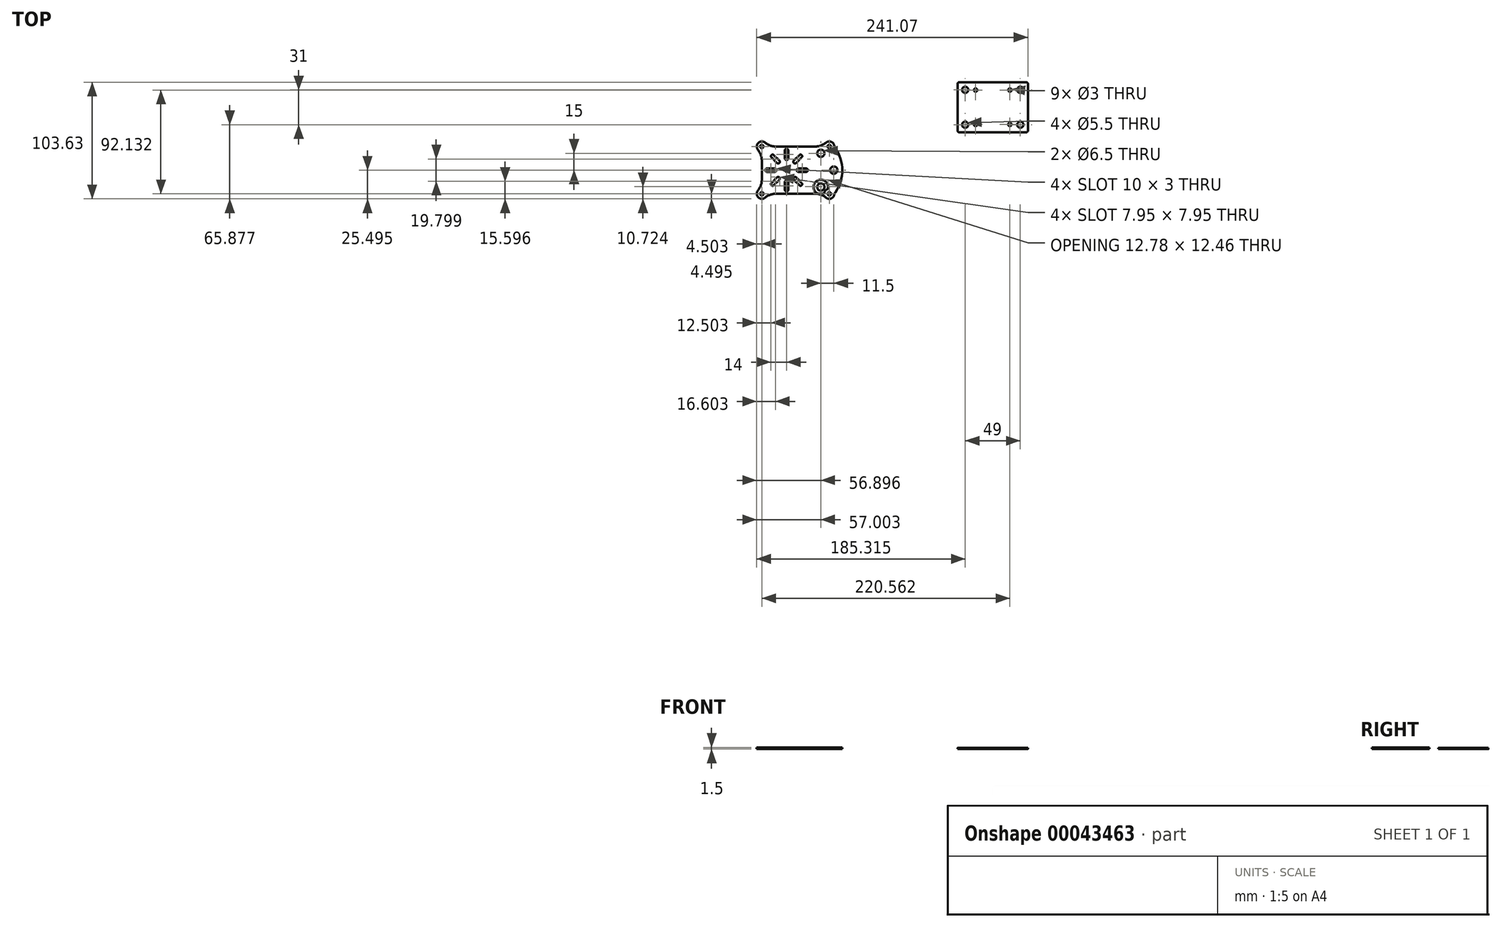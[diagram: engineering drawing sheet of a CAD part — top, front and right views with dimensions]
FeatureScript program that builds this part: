
annotation { "Feature Type Name" : "Feature", "Feature Type Description" : "" }
export const myFeature = defineFeature(function(context is Context, id is Id, definition is map)
    precondition{}
    {
        {
            var Q0;
            Q0=qCreatedBy(makeId("Top.planeOp"),FACE);
            var sketch = newSketch(context, id + "F0", { "sketchPlane" : qUnion([Q0])});
            skCircle(sketch, "E0", {"center": v(-51.28, 40.9) * mm, "radius": 1.5 * mm});
            skCircle(sketch, "E1", {"center": v(8.72, 40.9) * mm, "radius": 1.5 * mm});
            skCircle(sketch, "E2", {"center": v(-51.28, -1.1) * mm, "radius": 1.5 * mm});
            skCircle(sketch, "E3", {"center": v(8.72, -1.1) * mm, "radius": 1.5 * mm});
            skCircle(sketch, "E4", {"center": v(-29.28, 19.9) * mm, "radius": 27 * mm});
            skLineSegment(sketch, "E5", {"start": v(-51.28, 40.9) * mm, "end": v(-51.28, -1.1) * mm});
            skLineSegment(sketch, "E6", {"start": v(-51.28, 19.9) * mm, "end": v(20.22, 19.9) * mm});
            skCircle(sketch, "E7", {"center": v(12.72, 19.9) * mm, "radius": 3.25 * mm});
            skCircle(sketch, "E8", {"center": v(12.72, 19.9) * mm, "radius": 6.5 * mm});
            skCircle(sketch, "E9", {"center": v(-51.28, 40.9) * mm, "radius": 4.5 * mm});
            skCircle(sketch, "E10", {"center": v(-51.28, -1.1) * mm, "radius": 4.5 * mm});
            skCircle(sketch, "E11", {"center": v(8.72, -1.1) * mm, "radius": 4.5 * mm});
            skCircle(sketch, "E12", {"center": v(8.72, 40.9) * mm, "radius": 4.5 * mm});
            skLineSegment(sketch, "E13", {"start": v(-51.28, 40.9) * mm, "end": v(8.72, 40.9) * mm});
            skLineSegment(sketch, "E14", {"start": v(8.72, 40.9) * mm, "end": v(13.22, 40.9) * mm});
            skLineSegment(sketch, "E15", {"start": v(8.72, -1.1) * mm, "end": v(13.22, -1.1) * mm});
            skArc(sketch, "E16", {"start": v(13.22, -1.1) * mm, "mid": v(20.22, 19.9) * mm, "end": v(13.22, 40.9) * mm});
            skLineSegment(sketch, "E17", {"start": v(-51.28, -1.1) * mm, "end": v(8.72, -1.1) * mm});
            skCircle(sketch, "E18", {"center": v(20.37, 43.8) * mm, "radius": 7.5 * mm});
            skCircle(sketch, "E19", {"center": v(20.37, -4) * mm, "radius": 7.5 * mm});
            skCircle(sketch, "E20", {"center": v(-66.28, 28.44) * mm, "radius": 15 * mm});
            skCircle(sketch, "E21", {"center": v(-66.28, 11.36) * mm, "radius": 15 * mm});
            skCircle(sketch, "E22", {"center": v(-38.82, -16.1) * mm, "radius": 15 * mm});
            skCircle(sketch, "E23", {"center": v(-3.74, -16.1) * mm, "radius": 15 * mm});
            skCircle(sketch, "E24", {"center": v(-3.74, 55.9) * mm, "radius": 15 * mm});
            skCircle(sketch, "E25", {"center": v(-38.82, 55.9) * mm, "radius": 15 * mm});
            skLineSegment(sketch, "E26", {"start": v(-29.28, 19.9) * mm, "end": v(-29.28, 46.9) * mm});
            skLineSegment(sketch, "E27.bottom", {"start": v(-38.28, 19.9) * mm, "end": v(-48.28, 19.9) * mm});
            skLineSegment(sketch, "E27.top", {"start": v(-39.78, 21.4) * mm, "end": v(-46.78, 21.4) * mm});
            skLineSegment(sketch, "E27.left", {"start": v(-38.28, 19.9) * mm, "end": v(-38.28, 19.9) * mm});
            skLineSegment(sketch, "E27.right", {"start": v(-48.28, 19.9) * mm, "end": v(-48.28, 19.9) * mm});
            skLineSegment(sketch, "E28.bottom", {"start": v(-29.28, 38.9) * mm, "end": v(-29.28, 38.9) * mm});
            skLineSegment(sketch, "E28.top", {"start": v(-29.28, 28.9) * mm, "end": v(-29.28, 28.9) * mm});
            skLineSegment(sketch, "E28.left", {"start": v(-29.28, 38.9) * mm, "end": v(-29.28, 28.9) * mm});
            skLineSegment(sketch, "E28.right", {"start": v(-30.78, 37.4) * mm, "end": v(-30.78, 30.4) * mm});
            skLineSegment(sketch, "E29", {"start": v(-35.64, 26.26) * mm, "end": v(-35.64, 26.26) * mm});
            skLineSegment(sketch, "E30", {"start": v(-35.64, 28.38) * mm, "end": v(-40.6, 33.33) * mm});
            skLineSegment(sketch, "E31", {"start": v(-42.71, 33.33) * mm, "end": v(-42.71, 33.33) * mm});
            skLineSegment(sketch, "E32", {"start": v(-42.71, 31.2) * mm, "end": v(-37.76, 26.26) * mm});
            skPoint(sketch, "E33", {"position": v(-35.64, 26.26) * mm});
            skLineSegment(sketch, "E34.MirrorCS", {"start": v(-27.78, 37.4) * mm, "end": v(-27.78, 30.4) * mm});
            skLineSegment(sketch, "E35.MirrorCS", {"start": v(-22.91, 28.38) * mm, "end": v(-17.96, 33.33) * mm});
            skLineSegment(sketch, "E36.MirrorCS", {"start": v(-15.84, 33.33) * mm, "end": v(-15.84, 33.33) * mm});
            skLineSegment(sketch, "E37.MirrorCS", {"start": v(-15.84, 31.2) * mm, "end": v(-20.8, 26.26) * mm});
            skLineSegment(sketch, "E38.MirrorCS", {"start": v(-22.91, 26.26) * mm, "end": v(-22.91, 26.26) * mm});
            skLineSegment(sketch, "E39.MirrorCS", {"start": v(-20.28, 19.9) * mm, "end": v(-20.28, 19.9) * mm});
            skLineSegment(sketch, "E40.MirrorCS", {"start": v(-18.78, 21.4) * mm, "end": v(-11.78, 21.4) * mm});
            skLineSegment(sketch, "E41.MirrorCS", {"start": v(-10.28, 19.9) * mm, "end": v(-10.28, 19.9) * mm});
            skLineSegment(sketch, "E42.MirrorCS", {"start": v(-18.78, 18.4) * mm, "end": v(-11.78, 18.4) * mm});
            skLineSegment(sketch, "E43.MirrorCS", {"start": v(-22.91, 11.41) * mm, "end": v(-17.96, 6.46) * mm});
            skLineSegment(sketch, "E44.MirrorCS", {"start": v(-15.84, 6.46) * mm, "end": v(-15.84, 6.46) * mm});
            skLineSegment(sketch, "E45.MirrorCS", {"start": v(-22.91, 13.53) * mm, "end": v(-22.91, 13.53) * mm});
            skLineSegment(sketch, "E46.MirrorCS", {"start": v(-15.84, 8.58) * mm, "end": v(-20.8, 13.53) * mm});
            skLineSegment(sketch, "E47.MirrorCS", {"start": v(-29.28, 0.9) * mm, "end": v(-29.28, 0.9) * mm});
            skLineSegment(sketch, "E48.MirrorCS", {"start": v(-27.78, 2.4) * mm, "end": v(-27.78, 9.4) * mm});
            skLineSegment(sketch, "E49.MirrorCS", {"start": v(-29.28, 10.9) * mm, "end": v(-29.28, 10.9) * mm});
            skLineSegment(sketch, "E50.MirrorCS", {"start": v(-30.78, 2.4) * mm, "end": v(-30.78, 9.4) * mm});
            skLineSegment(sketch, "E51.MirrorCS", {"start": v(-35.64, 11.41) * mm, "end": v(-40.6, 6.46) * mm});
            skLineSegment(sketch, "E52.MirrorCS", {"start": v(-42.71, 8.58) * mm, "end": v(-37.76, 13.53) * mm});
            skLineSegment(sketch, "E53.MirrorCS", {"start": v(-42.71, 6.46) * mm, "end": v(-42.71, 6.46) * mm});
            skLineSegment(sketch, "E54.MirrorCS", {"start": v(-35.64, 13.53) * mm, "end": v(-35.64, 13.53) * mm});
            skLineSegment(sketch, "E55.MirrorCS", {"start": v(-39.78, 18.4) * mm, "end": v(-46.78, 18.4) * mm});
            skCircle(sketch, "E56", {"center": v(-29.28, 19.9) * mm, "radius": 1.5 * mm});
            skPoint(sketch, "E57.visualSharp", {"position": v(-41.65, 34.4) * mm});
            skArc(sketch, "E57.filletArc", {"start": v(-40.6, 33.33) * mm, "mid": v(-41.65, 33.77) * mm, "end": v(-42.71, 33.33) * mm});
            skPoint(sketch, "E58.visualSharp", {"position": v(-43.77, 32.27) * mm});
            skArc(sketch, "E58.filletArc", {"start": v(-42.71, 33.33) * mm, "mid": v(-43.15, 32.27) * mm, "end": v(-42.71, 31.2) * mm});
            skPoint(sketch, "E59.visualSharp", {"position": v(-34.58, 27.32) * mm});
            skArc(sketch, "E59.filletArc", {"start": v(-35.64, 26.26) * mm, "mid": v(-35.2, 27.32) * mm, "end": v(-35.64, 28.38) * mm});
            skPoint(sketch, "E60.visualSharp", {"position": v(-36.7, 25.2) * mm});
            skArc(sketch, "E60.filletArc", {"start": v(-37.76, 26.26) * mm, "mid": v(-36.7, 25.82) * mm, "end": v(-35.64, 26.26) * mm});
            skPoint(sketch, "E61.visualSharp", {"position": v(-30.78, 28.9) * mm});
            skArc(sketch, "E61.filletArc", {"start": v(-30.78, 30.4) * mm, "mid": v(-30.34, 29.33) * mm, "end": v(-29.28, 28.9) * mm});
            skPoint(sketch, "E62.visualSharp", {"position": v(-27.78, 28.9) * mm});
            skArc(sketch, "E62.filletArc", {"start": v(-29.28, 28.9) * mm, "mid": v(-28.22, 29.33) * mm, "end": v(-27.78, 30.4) * mm});
            skPoint(sketch, "E63.visualSharp", {"position": v(-27.78, 38.9) * mm});
            skArc(sketch, "E63.filletArc", {"start": v(-27.78, 37.4) * mm, "mid": v(-28.22, 38.46) * mm, "end": v(-29.28, 38.9) * mm});
            skPoint(sketch, "E64.visualSharp", {"position": v(-30.78, 38.9) * mm});
            skArc(sketch, "E64.filletArc", {"start": v(-29.28, 38.9) * mm, "mid": v(-30.34, 38.46) * mm, "end": v(-30.78, 37.4) * mm});
            skPoint(sketch, "E65.visualSharp", {"position": v(-16.9, 34.4) * mm});
            skArc(sketch, "E65.filletArc", {"start": v(-15.84, 33.33) * mm, "mid": v(-16.9, 33.77) * mm, "end": v(-17.96, 33.33) * mm});
            skPoint(sketch, "E66.visualSharp", {"position": v(-14.78, 32.27) * mm});
            skArc(sketch, "E66.filletArc", {"start": v(-15.84, 31.2) * mm, "mid": v(-15.4, 32.27) * mm, "end": v(-15.84, 33.33) * mm});
            skPoint(sketch, "E67.visualSharp", {"position": v(-23.97, 27.32) * mm});
            skArc(sketch, "E67.filletArc", {"start": v(-22.91, 28.38) * mm, "mid": v(-23.35, 27.32) * mm, "end": v(-22.91, 26.26) * mm});
            skPoint(sketch, "E68.visualSharp", {"position": v(-21.85, 25.2) * mm});
            skArc(sketch, "E68.filletArc", {"start": v(-22.91, 26.26) * mm, "mid": v(-21.85, 25.82) * mm, "end": v(-20.8, 26.26) * mm});
            skPoint(sketch, "E69.visualSharp", {"position": v(-20.28, 21.4) * mm});
            skArc(sketch, "E69.filletArc", {"start": v(-18.78, 21.4) * mm, "mid": v(-19.84, 20.96) * mm, "end": v(-20.28, 19.9) * mm});
            skPoint(sketch, "E70.visualSharp", {"position": v(-20.28, 18.4) * mm});
            skArc(sketch, "E70.filletArc", {"start": v(-20.28, 19.9) * mm, "mid": v(-19.84, 18.83) * mm, "end": v(-18.78, 18.4) * mm});
            skPoint(sketch, "E71.visualSharp", {"position": v(-10.28, 21.4) * mm});
            skArc(sketch, "E71.filletArc", {"start": v(-10.28, 19.9) * mm, "mid": v(-10.72, 20.96) * mm, "end": v(-11.78, 21.4) * mm});
            skPoint(sketch, "E72.visualSharp", {"position": v(-10.28, 18.4) * mm});
            skArc(sketch, "E72.filletArc", {"start": v(-11.78, 18.4) * mm, "mid": v(-10.72, 18.83) * mm, "end": v(-10.28, 19.9) * mm});
            skPoint(sketch, "E73.visualSharp", {"position": v(-21.85, 14.6) * mm});
            skArc(sketch, "E73.filletArc", {"start": v(-20.8, 13.53) * mm, "mid": v(-21.85, 13.97) * mm, "end": v(-22.91, 13.53) * mm});
            skPoint(sketch, "E74.visualSharp", {"position": v(-23.97, 12.47) * mm});
            skArc(sketch, "E74.filletArc", {"start": v(-22.91, 13.53) * mm, "mid": v(-23.35, 12.47) * mm, "end": v(-22.91, 11.41) * mm});
            skPoint(sketch, "E75.visualSharp", {"position": v(-14.78, 7.52) * mm});
            skArc(sketch, "E75.filletArc", {"start": v(-15.84, 6.46) * mm, "mid": v(-15.4, 7.52) * mm, "end": v(-15.84, 8.58) * mm});
            skPoint(sketch, "E76.visualSharp", {"position": v(-16.9, 5.4) * mm});
            skArc(sketch, "E76.filletArc", {"start": v(-17.96, 6.46) * mm, "mid": v(-16.9, 6.02) * mm, "end": v(-15.84, 6.46) * mm});
            skPoint(sketch, "E77.visualSharp", {"position": v(-27.78, 10.9) * mm});
            skArc(sketch, "E77.filletArc", {"start": v(-27.78, 9.4) * mm, "mid": v(-28.22, 10.46) * mm, "end": v(-29.28, 10.9) * mm});
            skPoint(sketch, "E78.visualSharp", {"position": v(-30.78, 10.9) * mm});
            skArc(sketch, "E78.filletArc", {"start": v(-29.28, 10.9) * mm, "mid": v(-30.34, 10.46) * mm, "end": v(-30.78, 9.4) * mm});
            skPoint(sketch, "E79.visualSharp", {"position": v(-30.78, 0.9) * mm});
            skArc(sketch, "E79.filletArc", {"start": v(-30.78, 2.4) * mm, "mid": v(-30.34, 1.33) * mm, "end": v(-29.28, 0.9) * mm});
            skPoint(sketch, "E80.visualSharp", {"position": v(-27.78, 0.9) * mm});
            skArc(sketch, "E80.filletArc", {"start": v(-29.28, 0.9) * mm, "mid": v(-28.22, 1.33) * mm, "end": v(-27.78, 2.4) * mm});
            skPoint(sketch, "E81.visualSharp", {"position": v(-36.7, 14.6) * mm});
            skArc(sketch, "E81.filletArc", {"start": v(-35.64, 13.53) * mm, "mid": v(-36.7, 13.97) * mm, "end": v(-37.76, 13.53) * mm});
            skPoint(sketch, "E82.visualSharp", {"position": v(-34.58, 12.47) * mm});
            skArc(sketch, "E82.filletArc", {"start": v(-35.64, 11.41) * mm, "mid": v(-35.2, 12.47) * mm, "end": v(-35.64, 13.53) * mm});
            skPoint(sketch, "E83.visualSharp", {"position": v(-43.77, 7.52) * mm});
            skArc(sketch, "E83.filletArc", {"start": v(-42.71, 8.58) * mm, "mid": v(-43.15, 7.52) * mm, "end": v(-42.71, 6.46) * mm});
            skPoint(sketch, "E84.visualSharp", {"position": v(-41.65, 5.4) * mm});
            skArc(sketch, "E84.filletArc", {"start": v(-42.71, 6.46) * mm, "mid": v(-41.65, 6.02) * mm, "end": v(-40.6, 6.46) * mm});
            skPoint(sketch, "E85.visualSharp", {"position": v(-48.28, 21.4) * mm});
            skArc(sketch, "E85.filletArc", {"start": v(-46.78, 21.4) * mm, "mid": v(-47.84, 20.96) * mm, "end": v(-48.28, 19.9) * mm});
            skPoint(sketch, "E86.visualSharp", {"position": v(-38.28, 21.4) * mm});
            skArc(sketch, "E86.filletArc", {"start": v(-38.28, 19.9) * mm, "mid": v(-38.72, 20.96) * mm, "end": v(-39.78, 21.4) * mm});
            skPoint(sketch, "E87.visualSharp", {"position": v(-38.28, 18.4) * mm});
            skArc(sketch, "E87.filletArc", {"start": v(-39.78, 18.4) * mm, "mid": v(-38.72, 18.83) * mm, "end": v(-38.28, 19.9) * mm});
            skPoint(sketch, "E88.visualSharp", {"position": v(-48.28, 18.4) * mm});
            skArc(sketch, "E88.filletArc", {"start": v(-48.28, 19.9) * mm, "mid": v(-47.84, 18.83) * mm, "end": v(-46.78, 18.4) * mm});
            skCircle(sketch, "E89", {"center": v(1.22, 34.9) * mm, "radius": 3.25 * mm});
            skCircle(sketch, "E90", {"center": v(1.22, 34.9) * mm, "radius": 6.5 * mm});
            skCircle(sketch, "E91.MirrorC", {"center": v(1.22, 4.9) * mm, "radius": 3.25 * mm});
            skCircle(sketch, "E92.MirrorC", {"center": v(1.22, 4.9) * mm, "radius": 6.5 * mm});
            skCircle(sketch, "E93", {"center": v(8.72, 40.9) * mm, "radius": 2.75 * mm});
            skSolve(sketch);
        }
        {
            var Q0;
            {var subQ1=sQuery(id+"F0.wireOp",EDGE,"E5");var subQ3=sQuery(id+"F0.wireOp",EDGE,"E4");var subQ4=makeQuery(id+"F0.imprint","INTERSECT",VERTEX,{"disambiguationData":[OD(1.0)],"derivedFrom":[subQ3,subQ1]});Q0=makeQuery(id+"F0.imprint","IMPRINT",FACE,{"disambiguationData":[TD([[makeQuery(id+"F0.imprint","IMPRINT",EDGE,{"disambiguationData":[TD([[subQ4,-1.0]])],"derivedFrom":subQ3}),1.0]])]});}
            var Q1;
            {var subQ4=sQuery(id+"F0.wireOp",EDGE,"E4");var subQ8=sQuery(id+"F0.wireOp",EDGE,"E13");var subQ9=makeQuery(id+"F0.imprint","INTERSECT",VERTEX,{"disambiguationData":[OD(0.0)],"derivedFrom":[subQ4,subQ8]});Q1=makeQuery(id+"F0.imprint","IMPRINT",FACE,{"disambiguationData":[TD([[makeQuery(id+"F0.imprint","IMPRINT",EDGE,{"disambiguationData":[TD([[subQ9,1.0]])],"derivedFrom":subQ4}),-1.0]])]});}
            var Q2;
            {var subQ4=sQuery(id+"F0.wireOp",EDGE,"E4");var subQ11=sQuery(id+"F0.wireOp",EDGE,"E17");var subQ12=makeQuery(id+"F0.imprint","INTERSECT",VERTEX,{"disambiguationData":[OD(0.0)],"derivedFrom":[subQ4,subQ11]});Q2=makeQuery(id+"F0.imprint","IMPRINT",FACE,{"disambiguationData":[TD([[makeQuery(id+"F0.imprint","IMPRINT",EDGE,{"disambiguationData":[TD([[subQ12,-1.0]])],"derivedFrom":subQ4}),-1.0]])]});}
            var Q3;
            {var subQ0=sQuery(id+"F0.wireOp",EDGE,"E8");var subQ1=sQuery(id+"F0.wireOp",EDGE,"E6");var subQ2=makeQuery(id+"F0.imprint","INTERSECT",VERTEX,{"disambiguationData":[OD(0.0)],"derivedFrom":[subQ1,subQ0]});Q3=makeQuery(id+"F0.imprint","IMPRINT",FACE,{"disambiguationData":[TD([[makeQuery(id+"F0.imprint","IMPRINT",EDGE,{"disambiguationData":[TD([[subQ2,-1.0]])],"derivedFrom":subQ1}),-1.0]])]});}
            var Q4;
            {var subQ0=sQuery(id+"F0.wireOp",EDGE,"E8");var subQ1=sQuery(id+"F0.wireOp",EDGE,"E6");var subQ2=makeQuery(id+"F0.imprint","INTERSECT",VERTEX,{"disambiguationData":[OD(0.0)],"derivedFrom":[subQ1,subQ0]});Q4=makeQuery(id+"F0.imprint","IMPRINT",FACE,{"disambiguationData":[TD([[makeQuery(id+"F0.imprint","IMPRINT",EDGE,{"disambiguationData":[TD([[subQ2,-1.0]])],"derivedFrom":subQ1}),1.0]])]});}
            var Q5;
            {var subQ0=sQuery(id+"F0.wireOp",EDGE,"E13");var subQ1=sQuery(id+"F0.wireOp",EDGE,"E1");var subQ2=makeQuery(id+"F0.imprint","INTERSECT",VERTEX,{"derivedFrom":[subQ1,subQ0]});Q5=makeQuery(id+"F0.imprint","IMPRINT",FACE,{"disambiguationData":[TD([[makeQuery(id+"F0.imprint","IMPRINT",EDGE,{"disambiguationData":[TD([[subQ2,-1.0]])],"derivedFrom":subQ1}),-1.0]])]});}
            var Q6;
            {var subQ2=sQuery(id+"F0.wireOp",EDGE,"E13");var subQ7=sQuery(id+"F0.wireOp",EDGE,"E1");var subQ9=makeQuery(id+"F0.imprint","INTERSECT",VERTEX,{"derivedFrom":[subQ7,subQ2]});Q6=makeQuery(id+"F0.imprint","IMPRINT",FACE,{"disambiguationData":[TD([[makeQuery(id+"F0.imprint","IMPRINT",EDGE,{"disambiguationData":[TD([[subQ9,1.0]])],"derivedFrom":subQ7}),-1.0]])]});}
            var Q7;
            {var subQ5=sQuery(id+"F0.wireOp",EDGE,"E5");var subQ6=sQuery(id+"F0.wireOp",EDGE,"E0");var subQ7=makeQuery(id+"F0.imprint","INTERSECT",VERTEX,{"derivedFrom":[subQ6,subQ5]});Q7=makeQuery(id+"F0.imprint","IMPRINT",FACE,{"disambiguationData":[TD([[makeQuery(id+"F0.imprint","IMPRINT",EDGE,{"disambiguationData":[TD([[subQ7,1.0]])],"derivedFrom":subQ6}),-1.0]])]});}
            var Q8;
            {var subQ0=sQuery(id+"F0.wireOp",EDGE,"E5");var subQ1=sQuery(id+"F0.wireOp",EDGE,"E0");var subQ2=makeQuery(id+"F0.imprint","INTERSECT",VERTEX,{"derivedFrom":[subQ1,subQ0]});Q8=makeQuery(id+"F0.imprint","IMPRINT",FACE,{"disambiguationData":[TD([[makeQuery(id+"F0.imprint","IMPRINT",EDGE,{"disambiguationData":[TD([[subQ2,-1.0]])],"derivedFrom":subQ1}),-1.0]])]});}
            var Q9;
            {var subQ0=sQuery(id+"F0.wireOp",EDGE,"E5");var subQ1=sQuery(id+"F0.wireOp",EDGE,"E2");var subQ2=makeQuery(id+"F0.imprint","INTERSECT",VERTEX,{"derivedFrom":[subQ1,subQ0]});Q9=makeQuery(id+"F0.imprint","IMPRINT",FACE,{"disambiguationData":[TD([[makeQuery(id+"F0.imprint","IMPRINT",EDGE,{"disambiguationData":[TD([[subQ2,1.0]])],"derivedFrom":subQ1}),-1.0]])]});}
            var Q10;
            {var subQ3=sQuery(id+"F0.wireOp",EDGE,"E5");var subQ5=sQuery(id+"F0.wireOp",EDGE,"E2");var subQ6=makeQuery(id+"F0.imprint","INTERSECT",VERTEX,{"derivedFrom":[subQ5,subQ3]});Q10=makeQuery(id+"F0.imprint","IMPRINT",FACE,{"disambiguationData":[TD([[makeQuery(id+"F0.imprint","IMPRINT",EDGE,{"disambiguationData":[TD([[subQ6,-1.0]])],"derivedFrom":subQ5}),-1.0]])]});}
            var Q11;
            {var subQ0=sQuery(id+"F0.wireOp",EDGE,"E15");var subQ5=sQuery(id+"F0.wireOp",EDGE,"E3");var subQ6=makeQuery(id+"F0.imprint","INTERSECT",VERTEX,{"derivedFrom":[subQ5,subQ0]});Q11=makeQuery(id+"F0.imprint","IMPRINT",FACE,{"disambiguationData":[TD([[makeQuery(id+"F0.imprint","IMPRINT",EDGE,{"disambiguationData":[TD([[subQ6,1.0]])],"derivedFrom":subQ5}),-1.0]])]});}
            var Q12;
            {var subQ0=sQuery(id+"F0.wireOp",EDGE,"E15");var subQ1=sQuery(id+"F0.wireOp",EDGE,"E3");var subQ2=makeQuery(id+"F0.imprint","INTERSECT",VERTEX,{"derivedFrom":[subQ1,subQ0]});Q12=makeQuery(id+"F0.imprint","IMPRINT",FACE,{"disambiguationData":[TD([[makeQuery(id+"F0.imprint","IMPRINT",EDGE,{"disambiguationData":[TD([[subQ2,-1.0]])],"derivedFrom":subQ1}),-1.0]])]});}
            var Q13;
            {var subQ0=sQuery(id+"F0.wireOp",EDGE,"E10");var subQ1=sQuery(id+"F0.wireOp",EDGE,"E4");var subQ2=makeQuery(id+"F0.imprint","INTERSECT",VERTEX,{"disambiguationData":[OD(0.0)],"derivedFrom":[subQ1,subQ0]});Q13=makeQuery(id+"F0.imprint","IMPRINT",FACE,{"disambiguationData":[TD([[makeQuery(id+"F0.imprint","IMPRINT",EDGE,{"disambiguationData":[TD([[subQ2,-1.0]])],"derivedFrom":subQ1}),1.0]])]});}
            var Q14;
            {var subQ0=sQuery(id+"F0.wireOp",EDGE,"E5");var subQ1=sQuery(id+"F0.wireOp",EDGE,"E4");var subQ2=makeQuery(id+"F0.imprint","INTERSECT",VERTEX,{"disambiguationData":[OD(1.0)],"derivedFrom":[subQ1,subQ0]});Q14=makeQuery(id+"F0.imprint","IMPRINT",FACE,{"disambiguationData":[TD([[makeQuery(id+"F0.imprint","IMPRINT",EDGE,{"disambiguationData":[TD([[subQ2,-1.0]])],"derivedFrom":subQ1}),-1.0]])]});}
            var Q15;
            {var subQ0=sQuery(id+"F0.wireOp",EDGE,"E17");var subQ1=sQuery(id+"F0.wireOp",EDGE,"E4");var subQ2=makeQuery(id+"F0.imprint","INTERSECT",VERTEX,{"disambiguationData":[OD(1.0)],"derivedFrom":[subQ1,subQ0]});Q15=makeQuery(id+"F0.imprint","IMPRINT",FACE,{"disambiguationData":[TD([[makeQuery(id+"F0.imprint","IMPRINT",EDGE,{"disambiguationData":[TD([[subQ2,-1.0]])],"derivedFrom":subQ1}),-1.0]])]});}
            var Q16;
            {var subQ0=sQuery(id+"F0.wireOp",EDGE,"E10");var subQ1=sQuery(id+"F0.wireOp",EDGE,"E4");var subQ2=makeQuery(id+"F0.imprint","INTERSECT",VERTEX,{"disambiguationData":[OD(1.0)],"derivedFrom":[subQ1,subQ0]});Q16=makeQuery(id+"F0.imprint","IMPRINT",FACE,{"disambiguationData":[TD([[makeQuery(id+"F0.imprint","IMPRINT",EDGE,{"disambiguationData":[TD([[subQ2,-1.0]])],"derivedFrom":subQ1}),-1.0]])]});}
            var Q17;
            {var subQ0=sQuery(id+"F0.wireOp",EDGE,"E5");var subQ1=sQuery(id+"F0.wireOp",EDGE,"E4");var subQ2=makeQuery(id+"F0.imprint","INTERSECT",VERTEX,{"disambiguationData":[OD(0.0)],"derivedFrom":[subQ1,subQ0]});Q17=makeQuery(id+"F0.imprint","IMPRINT",FACE,{"disambiguationData":[TD([[makeQuery(id+"F0.imprint","IMPRINT",EDGE,{"disambiguationData":[TD([[subQ2,-1.0]])],"derivedFrom":subQ1}),1.0]])]});}
            var Q18;
            {var subQ0=sQuery(id+"F0.wireOp",EDGE,"E5");var subQ1=sQuery(id+"F0.wireOp",EDGE,"E4");var subQ2=makeQuery(id+"F0.imprint","INTERSECT",VERTEX,{"disambiguationData":[OD(0.0)],"derivedFrom":[subQ1,subQ0]});Q18=makeQuery(id+"F0.imprint","IMPRINT",FACE,{"disambiguationData":[TD([[makeQuery(id+"F0.imprint","IMPRINT",EDGE,{"disambiguationData":[TD([[subQ2,-1.0]])],"derivedFrom":subQ1}),-1.0]])]});}
            var Q19;
            {var subQ0=sQuery(id+"F0.wireOp",EDGE,"E9");var subQ1=sQuery(id+"F0.wireOp",EDGE,"E4");var subQ2=makeQuery(id+"F0.imprint","INTERSECT",VERTEX,{"disambiguationData":[OD(0.0)],"derivedFrom":[subQ1,subQ0]});Q19=makeQuery(id+"F0.imprint","IMPRINT",FACE,{"disambiguationData":[TD([[makeQuery(id+"F0.imprint","IMPRINT",EDGE,{"disambiguationData":[TD([[subQ2,-1.0]])],"derivedFrom":subQ1}),1.0]])]});}
            var Q20;
            {var subQ0=sQuery(id+"F0.wireOp",EDGE,"E9");var subQ1=sQuery(id+"F0.wireOp",EDGE,"E4");var subQ2=makeQuery(id+"F0.imprint","INTERSECT",VERTEX,{"disambiguationData":[OD(1.0)],"derivedFrom":[subQ1,subQ0]});Q20=makeQuery(id+"F0.imprint","IMPRINT",FACE,{"disambiguationData":[TD([[makeQuery(id+"F0.imprint","IMPRINT",EDGE,{"disambiguationData":[TD([[subQ2,-1.0]])],"derivedFrom":subQ1}),-1.0]])]});}
            var Q21;
            {var subQ1=sQuery(id+"F0.wireOp",EDGE,"E4");var subQ6=sQuery(id+"F0.wireOp",EDGE,"E13");var subQ10=makeQuery(id+"F0.imprint","INTERSECT",VERTEX,{"disambiguationData":[OD(0.0)],"derivedFrom":[subQ1,subQ6]});Q21=makeQuery(id+"F0.imprint","IMPRINT",FACE,{"disambiguationData":[TD([[makeQuery(id+"F0.imprint","IMPRINT",EDGE,{"disambiguationData":[TD([[subQ10,1.0]])],"derivedFrom":subQ1}),1.0]])]});}
            var Q22;
            {var subQ0=sQuery(id+"F0.wireOp",EDGE,"E25");var subQ1=sQuery(id+"F0.wireOp",EDGE,"E4");var subQ2=makeQuery(id+"F0.imprint","INTERSECT",VERTEX,{"disambiguationData":[OD(1.0)],"derivedFrom":[subQ1,subQ0]});Q22=makeQuery(id+"F0.imprint","IMPRINT",FACE,{"disambiguationData":[TD([[makeQuery(id+"F0.imprint","IMPRINT",EDGE,{"disambiguationData":[TD([[subQ2,-1.0]])],"derivedFrom":subQ1}),-1.0]])]});}
            var Q23;
            {var subQ0=sQuery(id+"F0.wireOp",EDGE,"E25");var subQ1=sQuery(id+"F0.wireOp",EDGE,"E4");var subQ2=makeQuery(id+"F0.imprint","INTERSECT",VERTEX,{"disambiguationData":[OD(1.0)],"derivedFrom":[subQ1,subQ0]});Q23=makeQuery(id+"F0.imprint","IMPRINT",FACE,{"disambiguationData":[TD([[makeQuery(id+"F0.imprint","IMPRINT",EDGE,{"disambiguationData":[TD([[subQ2,-1.0]])],"derivedFrom":subQ1}),1.0]])]});}
            var Q24;
            {var subQ0=sQuery(id+"F0.wireOp",EDGE,"E13");var subQ1=sQuery(id+"F0.wireOp",EDGE,"E4");var subQ2=makeQuery(id+"F0.imprint","INTERSECT",VERTEX,{"disambiguationData":[OD(1.0)],"derivedFrom":[subQ1,subQ0]});Q24=makeQuery(id+"F0.imprint","IMPRINT",FACE,{"disambiguationData":[TD([[makeQuery(id+"F0.imprint","IMPRINT",EDGE,{"disambiguationData":[TD([[subQ2,-1.0]])],"derivedFrom":subQ1}),-1.0]])]});}
            var Q25;
            {var subQ0=sQuery(id+"F0.wireOp",EDGE,"E24");var subQ1=sQuery(id+"F0.wireOp",EDGE,"E12");var subQ2=makeQuery(id+"F0.imprint","INTERSECT",VERTEX,{"derivedFrom":[subQ1,subQ0]});Q25=makeQuery(id+"F0.imprint","IMPRINT",FACE,{"disambiguationData":[TD([[makeQuery(id+"F0.imprint","IMPRINT",EDGE,{"disambiguationData":[TD([[subQ2,-1.0]])],"derivedFrom":subQ1}),-1.0]])]});}
            var Q26;
            {var subQ1=sQuery(id+"F0.wireOp",EDGE,"E12");var subQ3=sQuery(id+"F0.wireOp",EDGE,"E18");var subQ4=makeQuery(id+"F0.imprint","INTERSECT",VERTEX,{"derivedFrom":[subQ1,subQ3]});Q26=makeQuery(id+"F0.imprint","IMPRINT",FACE,{"disambiguationData":[TD([[makeQuery(id+"F0.imprint","IMPRINT",EDGE,{"disambiguationData":[TD([[subQ4,-1.0]])],"derivedFrom":subQ3}),-1.0]])]});}
            var Q27;
            {var subQ0=sQuery(id+"F0.wireOp",EDGE,"E23");var subQ1=sQuery(id+"F0.wireOp",EDGE,"E11");var subQ2=makeQuery(id+"F0.imprint","INTERSECT",VERTEX,{"derivedFrom":[subQ1,subQ0]});Q27=makeQuery(id+"F0.imprint","IMPRINT",FACE,{"disambiguationData":[TD([[makeQuery(id+"F0.imprint","IMPRINT",EDGE,{"disambiguationData":[TD([[subQ2,1.0]])],"derivedFrom":subQ1}),-1.0]])]});}
            var Q28;
            {var subQ1=sQuery(id+"F0.wireOp",EDGE,"E11");var subQ3=sQuery(id+"F0.wireOp",EDGE,"E19");var subQ4=makeQuery(id+"F0.imprint","INTERSECT",VERTEX,{"derivedFrom":[subQ1,subQ3]});Q28=makeQuery(id+"F0.imprint","IMPRINT",FACE,{"disambiguationData":[TD([[makeQuery(id+"F0.imprint","IMPRINT",EDGE,{"disambiguationData":[TD([[subQ4,1.0]])],"derivedFrom":subQ3}),-1.0]])]});}
            var Q29;
            {var subQ0=sQuery(id+"F0.wireOp",EDGE,"E21");var subQ1=sQuery(id+"F0.wireOp",EDGE,"E4");var subQ2=makeQuery(id+"F0.imprint","INTERSECT",VERTEX,{"disambiguationData":[OD(1.0)],"derivedFrom":[subQ1,subQ0]});Q29=makeQuery(id+"F0.imprint","IMPRINT",FACE,{"disambiguationData":[TD([[makeQuery(id+"F0.imprint","IMPRINT",EDGE,{"disambiguationData":[TD([[subQ2,-1.0]])],"derivedFrom":subQ1}),-1.0]])]});}
            var Q30;
            {var subQ0=sQuery(id+"F0.wireOp",EDGE,"E21");var subQ1=sQuery(id+"F0.wireOp",EDGE,"E4");var subQ2=makeQuery(id+"F0.imprint","INTERSECT",VERTEX,{"disambiguationData":[OD(1.0)],"derivedFrom":[subQ1,subQ0]});Q30=makeQuery(id+"F0.imprint","IMPRINT",FACE,{"disambiguationData":[TD([[makeQuery(id+"F0.imprint","IMPRINT",EDGE,{"disambiguationData":[TD([[subQ2,-1.0]])],"derivedFrom":subQ1}),1.0]])]});}
            var Q31;
            {var subQ0=sQuery(id+"F0.wireOp",EDGE,"E17");var subQ1=sQuery(id+"F0.wireOp",EDGE,"E4");var subQ2=makeQuery(id+"F0.imprint","INTERSECT",VERTEX,{"disambiguationData":[OD(1.0)],"derivedFrom":[subQ1,subQ0]});Q31=makeQuery(id+"F0.imprint","IMPRINT",FACE,{"disambiguationData":[TD([[makeQuery(id+"F0.imprint","IMPRINT",EDGE,{"disambiguationData":[TD([[subQ2,-1.0]])],"derivedFrom":subQ1}),1.0]])]});}
            var Q32;
            Q32=makeQuery(id+"F0.imprint","IMPRINT",FACE,{"disambiguationData":[TD([[makeQuery(id+"F0.imprint","IMPRINT",EDGE,{"derivedFrom":sQuery(id+"F0.wireOp",EDGE,"E27.top")}),-1.0]])]});
            var Q33;
            Q33=makeQuery(id+"F0.imprint","IMPRINT",FACE,{"disambiguationData":[TD([[makeQuery(id+"F0.imprint","IMPRINT",EDGE,{"derivedFrom":sQuery(id+"F0.wireOp",EDGE,"E89")}),-1.0]])]});
            var Q34;
            {var subQ0=sQuery(id+"F0.wireOp",EDGE,"E90");var subQ1=sQuery(id+"F0.wireOp",EDGE,"E12");var subQ2=makeQuery(id+"F0.imprint","INTERSECT",VERTEX,{"disambiguationData":[OD(0.0)],"derivedFrom":[subQ1,subQ0]});Q34=makeQuery(id+"F0.imprint","IMPRINT",FACE,{"disambiguationData":[TD([[makeQuery(id+"F0.imprint","IMPRINT",EDGE,{"disambiguationData":[TD([[subQ2,-1.0]])],"derivedFrom":subQ1}),1.0]])]});}
            var Q35;
            {var subQ0=sQuery(id+"F0.wireOp",EDGE,"E90");var subQ1=sQuery(id+"F0.wireOp",EDGE,"E13");var subQ2=makeQuery(id+"F0.imprint","INTERSECT",VERTEX,{"disambiguationData":[OD(0.0)],"derivedFrom":[subQ1,subQ0]});Q35=makeQuery(id+"F0.imprint","IMPRINT",FACE,{"disambiguationData":[TD([[makeQuery(id+"F0.imprint","IMPRINT",EDGE,{"disambiguationData":[TD([[subQ2,-1.0]])],"derivedFrom":subQ1}),1.0]])]});}
            var Q36;
            {var subQ1=sQuery(id+"F0.wireOp",EDGE,"E12");var subQ6=makeQuery(id+"F0.imprint","INTERSECT",VERTEX,{"derivedFrom":[subQ1,sQuery(id+"F0.wireOp",EDGE,"E18")]});Q36=makeQuery(id+"F0.imprint","IMPRINT",FACE,{"disambiguationData":[TD([[makeQuery(id+"F0.imprint","IMPRINT",EDGE,{"disambiguationData":[TD([[subQ6,-1.0]])],"derivedFrom":subQ1}),1.0]])]});}
            var Q37;
            {var subQ1=sQuery(id+"F0.wireOp",EDGE,"E12");var subQ5=sQuery(id+"F0.wireOp",EDGE,"E13");var subQ6=makeQuery(id+"F0.imprint","INTERSECT",VERTEX,{"derivedFrom":[subQ1,subQ5]});Q37=makeQuery(id+"F0.imprint","IMPRINT",FACE,{"disambiguationData":[TD([[makeQuery(id+"F0.imprint","IMPRINT",EDGE,{"disambiguationData":[TD([[subQ6,-1.0]])],"derivedFrom":subQ1}),1.0]])]});}
            var Q38;
            {var subQ0=sQuery(id+"F0.wireOp",EDGE,"E13");var subQ1=sQuery(id+"F0.wireOp",EDGE,"E12");var subQ2=makeQuery(id+"F0.imprint","INTERSECT",VERTEX,{"derivedFrom":[subQ1,subQ0]});Q38=makeQuery(id+"F0.imprint","IMPRINT",FACE,{"disambiguationData":[TD([[makeQuery(id+"F0.imprint","IMPRINT",EDGE,{"disambiguationData":[TD([[subQ2,-1.0]])],"derivedFrom":subQ1}),-1.0]])]});}
            var Q39;
            Q39=makeQuery(id+"F0.imprint","IMPRINT",FACE,{"disambiguationData":[TD([[makeQuery(id+"F0.imprint","IMPRINT",EDGE,{"derivedFrom":sQuery(id+"F0.wireOp",EDGE,"E91.MirrorC")}),1.0]])]});
            var Q40;
            {var subQ0=sQuery(id+"F0.wireOp",EDGE,"E92.MirrorC");var subQ1=sQuery(id+"F0.wireOp",EDGE,"E11");var subQ2=makeQuery(id+"F0.imprint","INTERSECT",VERTEX,{"disambiguationData":[OD(0.0)],"derivedFrom":[subQ1,subQ0]});Q40=makeQuery(id+"F0.imprint","IMPRINT",FACE,{"disambiguationData":[TD([[makeQuery(id+"F0.imprint","IMPRINT",EDGE,{"disambiguationData":[TD([[subQ2,-1.0]])],"derivedFrom":subQ1}),1.0]])]});}
            var Q41;
            {var subQ0=sQuery(id+"F0.wireOp",EDGE,"E92.MirrorC");var subQ1=sQuery(id+"F0.wireOp",EDGE,"E11");var subQ2=makeQuery(id+"F0.imprint","INTERSECT",VERTEX,{"disambiguationData":[OD(1.0)],"derivedFrom":[subQ1,subQ0]});Q41=makeQuery(id+"F0.imprint","IMPRINT",FACE,{"disambiguationData":[TD([[makeQuery(id+"F0.imprint","IMPRINT",EDGE,{"disambiguationData":[TD([[subQ2,-1.0]])],"derivedFrom":subQ1}),-1.0]])]});}
            var Q42;
            {var subQ0=sQuery(id+"F0.wireOp",EDGE,"E92.MirrorC");var subQ1=sQuery(id+"F0.wireOp",EDGE,"E17");var subQ2=makeQuery(id+"F0.imprint","INTERSECT",VERTEX,{"disambiguationData":[OD(0.0)],"derivedFrom":[subQ1,subQ0]});Q42=makeQuery(id+"F0.imprint","IMPRINT",FACE,{"disambiguationData":[TD([[makeQuery(id+"F0.imprint","IMPRINT",EDGE,{"disambiguationData":[TD([[subQ2,-1.0]])],"derivedFrom":subQ1}),-1.0]])]});}
            extrude(context, id + "F1", {"entities" : qUnion([Q0, Q1, Q2, Q3, Q4, Q5, Q6, Q7, Q8, Q9, Q10, Q11, Q12, Q13, Q14, Q15, Q16, Q17, Q18, Q19, Q20, Q21, Q22, Q23, Q24, Q25, Q26, Q27, Q28, Q29, Q30, Q31, Q32, Q33, Q34, Q35, Q36, Q37, Q38, Q39, Q40, Q41, Q42]), "depth" : 1.5 * mm});
        }
        {
            var Q0;
            Q0=qCreatedBy(makeId("Top.planeOp"),FACE);
            var sketch = newSketch(context, id + "F2", { "sketchPlane" : qUnion([Q0])});
            skCircle(sketch, "E94", {"center": v(129.54, 91.28) * mm, "radius": 2.75 * mm});
            skCircle(sketch, "E95", {"center": v(178.54, 91.28) * mm, "radius": 2.75 * mm});
            skCircle(sketch, "E96", {"center": v(129.54, 60.28) * mm, "radius": 2.75 * mm});
            skCircle(sketch, "E97", {"center": v(178.54, 60.28) * mm, "radius": 2.75 * mm});
            skLineSegment(sketch, "E98.bottom", {"start": v(124.29, 98.03) * mm, "end": v(183.79, 98.03) * mm});
            skLineSegment(sketch, "E98.top", {"start": v(124.29, 53.53) * mm, "end": v(183.79, 53.53) * mm});
            skLineSegment(sketch, "E98.left", {"start": v(122.79, 96.53) * mm, "end": v(122.79, 55.03) * mm});
            skLineSegment(sketch, "E98.right", {"start": v(185.29, 96.53) * mm, "end": v(185.29, 55.03) * mm});
            skPoint(sketch, "E99.visualSharp", {"position": v(122.79, 98.03) * mm});
            skArc(sketch, "E99.filletArc", {"start": v(124.29, 98.03) * mm, "mid": v(123.22, 97.59) * mm, "end": v(122.79, 96.53) * mm});
            skPoint(sketch, "E100.visualSharp", {"position": v(185.29, 98.03) * mm});
            skArc(sketch, "E100.filletArc", {"start": v(185.29, 96.53) * mm, "mid": v(184.85, 97.59) * mm, "end": v(183.79, 98.03) * mm});
            skPoint(sketch, "E101.visualSharp", {"position": v(185.29, 53.53) * mm});
            skArc(sketch, "E101.filletArc", {"start": v(183.79, 53.53) * mm, "mid": v(184.85, 53.97) * mm, "end": v(185.29, 55.03) * mm});
            skPoint(sketch, "E102.visualSharp", {"position": v(122.79, 53.53) * mm});
            skArc(sketch, "E102.filletArc", {"start": v(122.79, 55.03) * mm, "mid": v(123.22, 53.97) * mm, "end": v(124.29, 53.53) * mm});
            skCircle(sketch, "E103", {"center": v(138.79, 91.03) * mm, "radius": 1.5 * mm});
            skCircle(sketch, "E104", {"center": v(169.29, 91.03) * mm, "radius": 1.5 * mm});
            skCircle(sketch, "E105", {"center": v(169.29, 60.53) * mm, "radius": 1.5 * mm});
            skCircle(sketch, "E106", {"center": v(138.79, 60.53) * mm, "radius": 1.5 * mm});
            skSolve(sketch);
        }
        {
            var Q0;
            Q0=makeQuery(id+"F2.imprint","IMPRINT",FACE,{"disambiguationData":[TD([[makeQuery(id+"F2.imprint","IMPRINT",EDGE,{"derivedFrom":sQuery(id+"F2.wireOp",EDGE,"E94")}),-1.0]])]});
            var Q1;
            Q1=makeQuery(id+"F2.imprint","IMPRINT",FACE,{"disambiguationData":[TD([[makeQuery(id+"F2.imprint","IMPRINT",EDGE,{"derivedFrom":sQuery(id+"F2.wireOp",EDGE,"E96")}),-1.0]])]});
            extrude(context, id + "F3", {"entities" : qUnion([Q0, Q1]), "depth" : 1 * mm});
        }
    });
